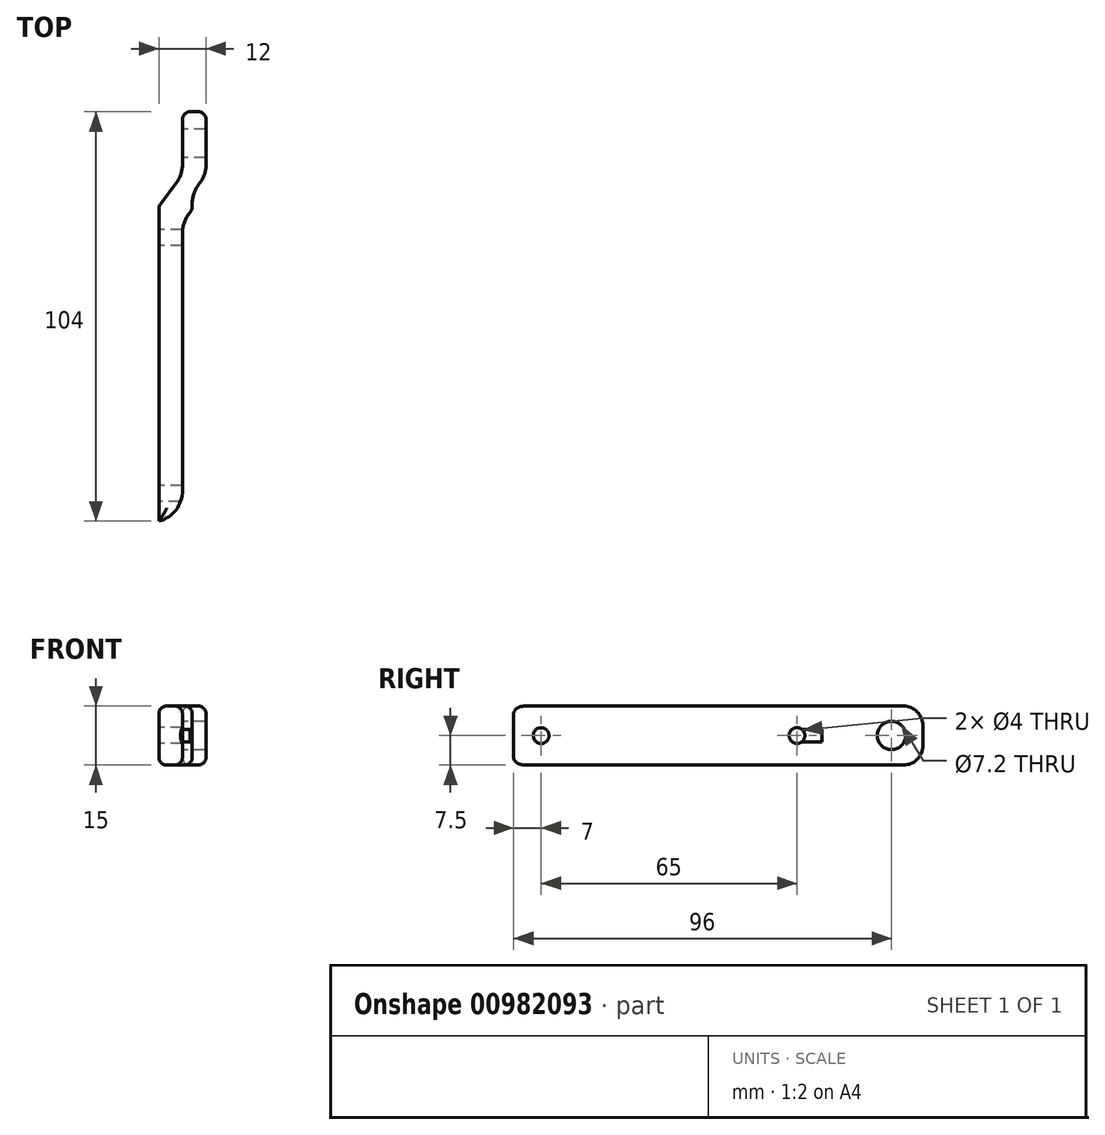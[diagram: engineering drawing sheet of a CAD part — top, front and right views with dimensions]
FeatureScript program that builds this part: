
annotation { "Feature Type Name" : "Feature", "Feature Type Description" : "" }
export const myFeature = defineFeature(function(context is Context, id is Id, definition is map)
    precondition{}
    {
        {
            var Q0;
            Q0=qCreatedBy(makeId("Top.planeOp"),FACE);
            var sketch = newSketch(context, id + "F0", { "sketchPlane" : qUnion([Q0])});
            skLineSegment(sketch, "E0.bottom", {"start": v(-6, 16) * mm, "end": v(0, 16) * mm});
            skLineSegment(sketch, "E0.left", {"start": v(-6, 16) * mm, "end": v(-6, 0) * mm});
            skLineSegment(sketch, "E0.right", {"start": v(0, 16) * mm, "end": v(0, 0) * mm});
            skLineSegment(sketch, "E1.top", {"start": v(-12, -88) * mm, "end": v(-6, -88) * mm});
            skLineSegment(sketch, "E1.left", {"start": v(-12, -8) * mm, "end": v(-12, -88) * mm});
            skLineSegment(sketch, "E1.right", {"start": v(-6, -10.5) * mm, "end": v(-6, -88) * mm});
            skLineSegment(sketch, "E2", {"start": v(0, 0) * mm, "end": v(-4.5, -6) * mm});
            skLineSegment(sketch, "E3", {"start": v(-6, 0) * mm, "end": v(-12, -8) * mm});
            skLineSegment(sketch, "E4", {"start": v(-6, -8) * mm, "end": v(-25.64, -8) * mm, "construction": true});
            skArc(sketch, "E5", {"start": v(-6, -10.5) * mm, "mid": v(-3.63, -8.8) * mm, "end": v(-4.5, -6) * mm});
            skSolve(sketch);
        }
        {
            var Q0;
            Q0 = qSketchRegion(id + "F0", true);
            extrude(context, id + "F1", {"entities" : qUnion([Q0]), "depth" : 15 * mm, "offsetDistance" : 25 * mm});
        }
        {
            var Q0;
            Q0=makeQuery(id+"F1.opExtrude","SWEPT_FACE",FACE,{"disambiguationData":[OSD([sQuery(id+"F0.wireOp",EDGE,"E0.left")])]});
            var sketch = newSketch(context, id + "F2", { "sketchPlane" : qUnion([Q0])});
            skLineSegment(sketch, "E6", {"start": v(-16, 7.5) * mm, "end": v(-1.81, 7.5) * mm, "construction": true});
            skLineSegment(sketch, "E7", {"start": v(-8, 15) * mm, "end": v(-8, 0) * mm, "construction": true});
            skPoint(sketch, "E8", {"position": v(-8, 7.5) * mm});
            skCircle(sketch, "E9", {"center": v(-8, 7.5) * mm, "radius": 3.6 * mm});
            skSolve(sketch);
        }
        {
            var Q0;
            Q0=makeQuery(id+"F2.imprint","IMPRINT",FACE,{"disambiguationData":[TD([[makeQuery(id+"F2.imprint","IMPRINT",EDGE,{"derivedFrom":sQuery(id+"F2.wireOp",EDGE,"E9")}),1.0]])]});
            extrude(context, id + "F3", {"entities" : qUnion([Q0]), "operationType" : NewBodyOperationType.REMOVE, "endBound" : BoundingType.UP_TO_NEXT, "oppositeDirection" : true, "depth" : 25 * mm, "offsetDistance" : 25 * mm});
        }
        {
            var Q0;
            Q0=makeQuery(id+"F1.opExtrude","SWEPT_FACE",FACE,{"disambiguationData":[OSD([sQuery(id+"F0.wireOp",EDGE,"E1.left")])]});
            var sketch = newSketch(context, id + "F4", { "sketchPlane" : qUnion([Q0])});
            skLineSegment(sketch, "E10", {"start": v(8, 7.5) * mm, "end": v(113, 7.5) * mm, "construction": true});
            skPoint(sketch, "E11", {"position": v(16, 7.5) * mm});
            skCircle(sketch, "E12", {"center": v(16, 7.5) * mm, "radius": 2 * mm});
            skPoint(sketch, "E13", {"position": v(81, 7.5) * mm});
            skCircle(sketch, "E14", {"center": v(81, 7.5) * mm, "radius": 2 * mm});
            skSolve(sketch);
        }
        {
            var Q0;
            Q0=makeQuery(id+"F4.imprint","IMPRINT",FACE,{"disambiguationData":[TD([[makeQuery(id+"F4.imprint","IMPRINT",EDGE,{"derivedFrom":sQuery(id+"F4.wireOp",EDGE,"E12")}),1.0]])]});
            var Q1;
            Q1=makeQuery(id+"F4.imprint","IMPRINT",FACE,{"disambiguationData":[TD([[makeQuery(id+"F4.imprint","IMPRINT",EDGE,{"derivedFrom":sQuery(id+"F4.wireOp",EDGE,"E14")}),1.0]])]});
            extrude(context, id + "F5", {"entities" : qUnion([Q0, Q1]), "operationType" : NewBodyOperationType.REMOVE, "endBound" : BoundingType.UP_TO_NEXT, "oppositeDirection" : true, "depth" : 25 * mm, "offsetDistance" : 25 * mm});
        }
        {
            var Q0;
            Q0=makeQuery(id+"F1.opExtrude","SWEPT_EDGE",EDGE,{"disambiguationData":[OSD([sQuery(id+"F0.wireOp",EDGE,"E0.left"),sQuery(id+"F0.wireOp",EDGE,"E3")])]});
            var Q1;
            Q1=makeQuery(id+"F1.opExtrude","SWEPT_EDGE",EDGE,{"disambiguationData":[OSD([sQuery(id+"F0.wireOp",EDGE,"E1.right"),sQuery(id+"F0.wireOp",EDGE,"E2")])]});
            fillet(context, id + "F6", {"entities" : qUnion([Q0, Q1]), "radius" : 8 * mm, "tangentPropagation" : true, "allowEdgeOverflow" : false});
        }
        {
            var Q0;
            Q0=makeQuery(id+"F1.opExtrude","SWEPT_EDGE",EDGE,{"disambiguationData":[OSD([sQuery(id+"F0.wireOp",EDGE,"E1.left"),sQuery(id+"F0.wireOp",EDGE,"E3")])]});
            var Q1;
            Q1=makeQuery(id+"F1.opExtrude","SWEPT_EDGE",EDGE,{"disambiguationData":[OSD([sQuery(id+"F0.wireOp",EDGE,"E0.right"),sQuery(id+"F0.wireOp",EDGE,"E2")])]});
            fillet(context, id + "F7", {"entities" : qUnion([Q0, Q1]), "radius" : 2 * mm, "tangentPropagation" : true, "allowEdgeOverflow" : false});
        }
        {
            var Q0;
            Q0=makeQuery(id+"F1.opExtrude","CAP_EDGE",EDGE,{"disambiguationData":[OSD([sQuery(id+"F0.wireOp",EDGE,"E0.bottom")])],"isStart":true});
            var Q1;
            Q1=makeQuery(id+"F1.opExtrude","CAP_EDGE",EDGE,{"disambiguationData":[OSD([sQuery(id+"F0.wireOp",EDGE,"E0.bottom")])],"isStart":false});
            var Q2;
            Q2=makeQuery(id+"F1.opExtrude","CAP_EDGE",EDGE,{"disambiguationData":[OSD([sQuery(id+"F0.wireOp",EDGE,"E1.top")])],"isStart":false});
            var Q3;
            Q3=makeQuery(id+"F1.opExtrude","CAP_EDGE",EDGE,{"disambiguationData":[OSD([sQuery(id+"F0.wireOp",EDGE,"E1.top")])],"isStart":true});
            fillet(context, id + "F8", {"entities" : qUnion([Q0, Q1, Q2, Q3]), "radius" : 5 * mm, "tangentPropagation" : true, "allowEdgeOverflow" : false});
        }
        {
            var Q0;
            Q0=makeQuery(id+"F1.opExtrude","CAP_EDGE",EDGE,{"disambiguationData":[OSD([sQuery(id+"F0.wireOp",EDGE,"E1.left")])],"isStart":true});
            var Q1;
            Q1=makeQuery(id+"F1.opExtrude","CAP_EDGE",EDGE,{"disambiguationData":[OSD([sQuery(id+"F0.wireOp",EDGE,"E1.right")])],"isStart":true});
            var Q2;
            Q2=makeQuery(id+"F1.opExtrude","CAP_EDGE",EDGE,{"disambiguationData":[OSD([sQuery(id+"F0.wireOp",EDGE,"E1.left")])],"isStart":false});
            var Q3;
            Q3=makeQuery(id+"F1.opExtrude","CAP_EDGE",EDGE,{"disambiguationData":[OSD([sQuery(id+"F0.wireOp",EDGE,"E1.right")])],"isStart":false});
            fillet(context, id + "F9", {"entities" : qUnion([Q0, Q1, Q2, Q3]), "radius" : 2 * mm, "tangentPropagation" : true, "allowEdgeOverflow" : false});
        }
    });
